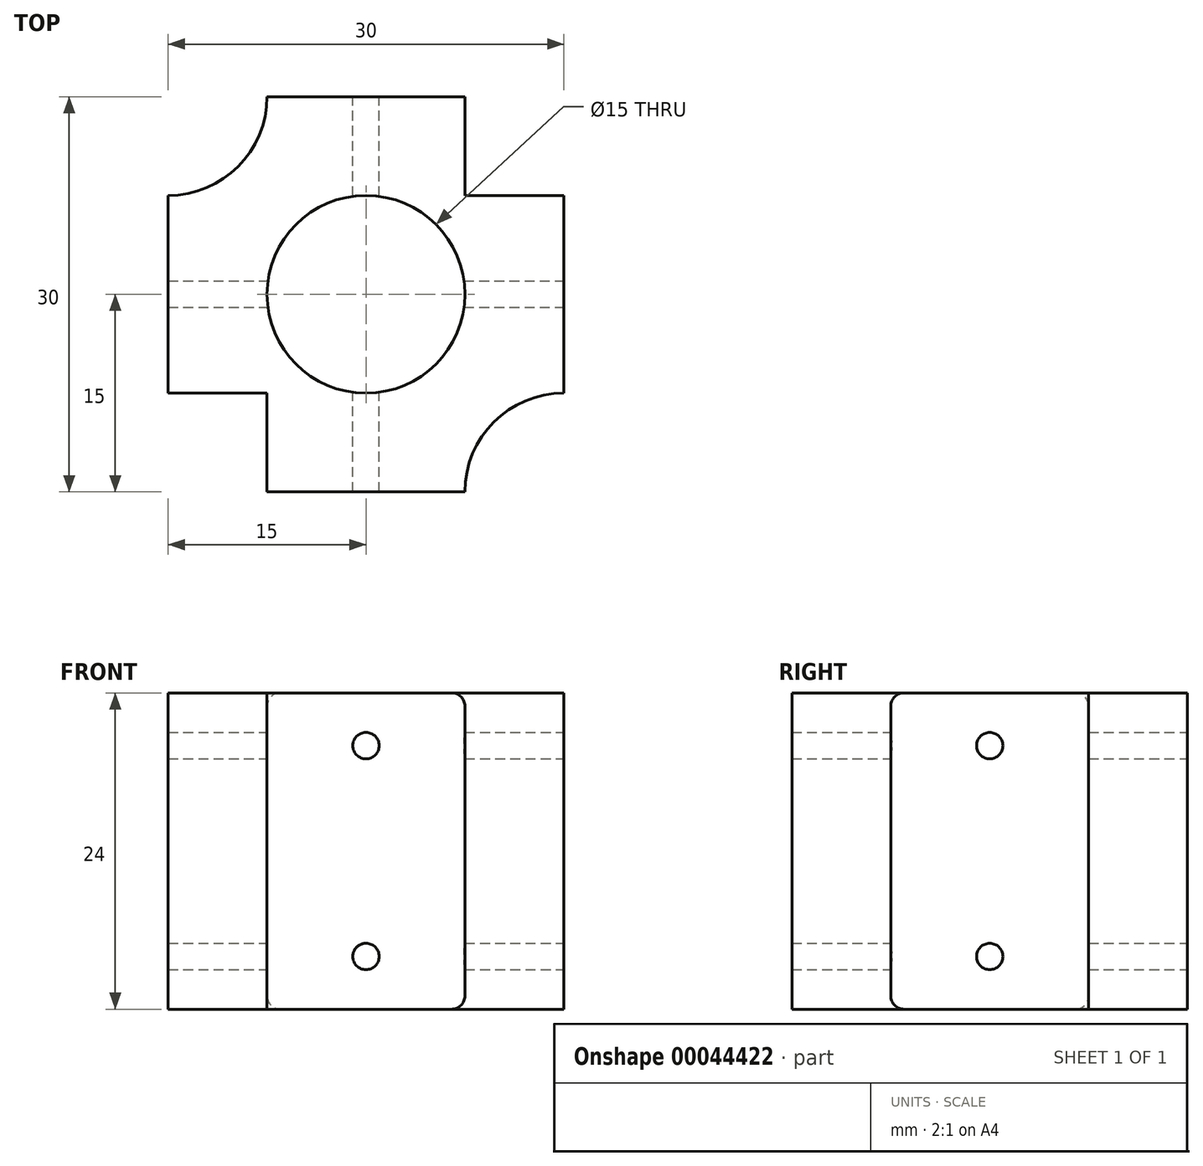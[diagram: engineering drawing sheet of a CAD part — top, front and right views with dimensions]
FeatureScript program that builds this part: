
annotation { "Feature Type Name" : "Feature", "Feature Type Description" : "" }
export const myFeature = defineFeature(function(context is Context, id is Id, definition is map)
    precondition{}
    {
        {
            var Q0;
            Q0=qCreatedBy(makeId("Top.planeOp"),FACE);
            var sketch = newSketch(context, id + "F0", { "sketchPlane" : qUnion([Q0])});
            skLineSegment(sketch, "E0.rect.bottom", {"start": v(15, -7.5) * mm, "end": v(-15, -7.5) * mm});
            skLineSegment(sketch, "E0.rect.top", {"start": v(15, 7.5) * mm, "end": v(-15, 7.5) * mm});
            skLineSegment(sketch, "E0.rect.left", {"start": v(15, -7.5) * mm, "end": v(15, 7.5) * mm});
            skLineSegment(sketch, "E0.rect.right", {"start": v(-15, -7.5) * mm, "end": v(-15, 7.5) * mm});
            skPoint(sketch, "E0.rect.middle", {"position": v(0, 0) * mm});
            skLineSegment(sketch, "E1.rect.bottom", {"start": v(7.5, 15) * mm, "end": v(-7.5, 15) * mm});
            skLineSegment(sketch, "E1.rect.top", {"start": v(7.5, -15) * mm, "end": v(-7.5, -15) * mm});
            skLineSegment(sketch, "E1.rect.left", {"start": v(7.5, 15) * mm, "end": v(7.5, -15) * mm});
            skLineSegment(sketch, "E1.rect.right", {"start": v(-7.5, 15) * mm, "end": v(-7.5, -15) * mm});
            skArc(sketch, "E2", {"start": v(-15, 7.5) * mm, "mid": v(-9.7, 9.7) * mm, "end": v(-7.5, 15) * mm});
            skArc(sketch, "E3.MirrorCS", {"start": v(15, 7.5) * mm, "mid": v(9.7, 9.7) * mm, "end": v(7.5, 15) * mm});
            skArc(sketch, "E4.MirrorCS", {"start": v(-15, -7.5) * mm, "mid": v(-9.7, -9.7) * mm, "end": v(-7.5, -15) * mm});
            skArc(sketch, "E5.MirrorCS", {"start": v(15, -7.5) * mm, "mid": v(9.7, -9.7) * mm, "end": v(7.5, -15) * mm});
            skSolve(sketch);
        }
        {
            var Q0;
            {var subQ0=sQuery(id+"F0.wireOp",EDGE,"E2");Q0=makeQuery(id+"F0.imprint","IMPRINT",FACE,{"disambiguationData":[TD([[makeQuery(id+"F0.imprint","IMPRINT",EDGE,{"derivedFrom":subQ0}),-1.0]])]});}
            var Q1;
            {var subQ3=sQuery(id+"F0.wireOp",EDGE,"E1.rect.bottom");Q1=makeQuery(id+"F0.imprint","IMPRINT",FACE,{"disambiguationData":[TD([[makeQuery(id+"F0.imprint","IMPRINT",EDGE,{"derivedFrom":subQ3}),1.0]])]});}
            var Q2;
            {var subQ3=sQuery(id+"F0.wireOp",EDGE,"E3.MirrorCS");Q2=makeQuery(id+"F0.imprint","IMPRINT",FACE,{"disambiguationData":[TD([[makeQuery(id+"F0.imprint","IMPRINT",EDGE,{"derivedFrom":subQ3}),1.0]])]});}
            var Q3;
            {var subQ5=sQuery(id+"F0.wireOp",EDGE,"E0.rect.left");Q3=makeQuery(id+"F0.imprint","IMPRINT",FACE,{"disambiguationData":[TD([[makeQuery(id+"F0.imprint","IMPRINT",EDGE,{"derivedFrom":subQ5}),1.0]])]});}
            var Q4;
            {var subQ3=sQuery(id+"F0.wireOp",EDGE,"E1.rect.top");Q4=makeQuery(id+"F0.imprint","IMPRINT",FACE,{"disambiguationData":[TD([[makeQuery(id+"F0.imprint","IMPRINT",EDGE,{"derivedFrom":subQ3}),-1.0]])]});}
            var Q5;
            {var subQ0=sQuery(id+"F0.wireOp",EDGE,"E5.MirrorCS");Q5=makeQuery(id+"F0.imprint","IMPRINT",FACE,{"disambiguationData":[TD([[makeQuery(id+"F0.imprint","IMPRINT",EDGE,{"derivedFrom":subQ0}),-1.0]])]});}
            var Q6;
            {var subQ3=sQuery(id+"F0.wireOp",EDGE,"E4.MirrorCS");Q6=makeQuery(id+"F0.imprint","IMPRINT",FACE,{"disambiguationData":[TD([[makeQuery(id+"F0.imprint","IMPRINT",EDGE,{"derivedFrom":subQ3}),1.0]])]});}
            var Q7;
            {var subQ5=sQuery(id+"F0.wireOp",EDGE,"E0.rect.right");Q7=makeQuery(id+"F0.imprint","IMPRINT",FACE,{"disambiguationData":[TD([[makeQuery(id+"F0.imprint","IMPRINT",EDGE,{"derivedFrom":subQ5}),-1.0]])]});}
            var Q8;
            {var subQ3=sQuery(id+"F0.wireOp",EDGE,"E0.rect.bottom");var subQ5=sQuery(id+"F0.wireOp",EDGE,"E1.rect.left");var subQ7=makeQuery(id+"F0.imprint","INTERSECT",VERTEX,{"derivedFrom":[subQ3,subQ5]});Q8=makeQuery(id+"F0.imprint","IMPRINT",FACE,{"disambiguationData":[TD([[makeQuery(id+"F0.imprint","IMPRINT",EDGE,{"disambiguationData":[TD([[subQ7,-1.0]])],"derivedFrom":subQ3}),-1.0]])]});}
            extrude(context, id + "F1", {"entities" : qUnion([Q0, Q1, Q2, Q3, Q4, Q5, Q6, Q7, Q8]), "depth" : 24 * mm, "symmetric" : true});
        }
        {
            var Q0;
            Q0=makeQuery(id+"F1.opExtrude","SWEPT_FACE",FACE,{"disambiguationData":[OSD([sQuery(id+"F0.wireOp",EDGE,"E1.rect.top")])]});
            var sketch = newSketch(context, id + "F2", { "sketchPlane" : qUnion([Q0])});
            skPoint(sketch, "E6", {"position": v(0, 8) * mm});
            skPoint(sketch, "E7.MirrorP", {"position": v(0, -8) * mm});
            skSolve(sketch);
        }
        {
            var Q0;
            Q0=sQuery(id+"F2.wireOp",VERTEX,"E6");
            var Q1;
            Q1=sQuery(id+"F2.wireOp",VERTEX,"E7.MirrorP");
            var Q2;
            Q2=makeQuery(id+"F1.opExtrude","SWEPT_BODY",BODY,{"disambiguationData":[OSD([sQuery(id+"F0.wireOp",EDGE,"E0.rect.left"),sQuery(id+"F0.wireOp",EDGE,"E0.rect.right"),sQuery(id+"F0.wireOp",EDGE,"E1.rect.bottom"),sQuery(id+"F0.wireOp",EDGE,"E1.rect.top"),sQuery(id+"F0.wireOp",EDGE,"E2"),sQuery(id+"F0.wireOp",EDGE,"E3.MirrorCS"),sQuery(id+"F0.wireOp",EDGE,"E4.MirrorCS"),sQuery(id+"F0.wireOp",EDGE,"E5.MirrorCS")])]});
            hole(context, id + "F3", {"style" : HoleStyle.SIMPLE, "holeDiameter" : 2 * mm, "endStyle" : HoleEndStyle.THROUGH, "locations" : qUnion([Q0, Q1]), "scope" : qUnion([Q2])});
        }
        {
            var Q0;
            Q0=makeQuery(id+"F1.opExtrude","CAP_FACE",FACE,{"disambiguationData":[OSD([sQuery(id+"F0.wireOp",EDGE,"E0.rect.left"),sQuery(id+"F0.wireOp",EDGE,"E0.rect.right"),sQuery(id+"F0.wireOp",EDGE,"E1.rect.bottom"),sQuery(id+"F0.wireOp",EDGE,"E1.rect.top"),sQuery(id+"F0.wireOp",EDGE,"E2"),sQuery(id+"F0.wireOp",EDGE,"E3.MirrorCS"),sQuery(id+"F0.wireOp",EDGE,"E4.MirrorCS"),sQuery(id+"F0.wireOp",EDGE,"E5.MirrorCS")])],"isStart":false});
            var sketch = newSketch(context, id + "F4", { "sketchPlane" : qUnion([Q0])});
            skPoint(sketch, "E8.0", {"position": v(0, 0) * mm});
            skSolve(sketch);
        }
        {
            var Q0;
            Q0=sQuery(id+"F4.wireOp",VERTEX,"E8.0");
            var Q1;
            Q1=makeQuery(id+"F1.opExtrude","SWEPT_BODY",BODY,{"disambiguationData":[OSD([sQuery(id+"F0.wireOp",EDGE,"E0.rect.left"),sQuery(id+"F0.wireOp",EDGE,"E0.rect.right"),sQuery(id+"F0.wireOp",EDGE,"E1.rect.bottom"),sQuery(id+"F0.wireOp",EDGE,"E1.rect.top"),sQuery(id+"F0.wireOp",EDGE,"E2"),sQuery(id+"F0.wireOp",EDGE,"E3.MirrorCS"),sQuery(id+"F0.wireOp",EDGE,"E4.MirrorCS"),sQuery(id+"F0.wireOp",EDGE,"E5.MirrorCS")])]});
            hole(context, id + "F5", {"style" : HoleStyle.SIMPLE, "holeDiameter" : 15 * mm, "endStyle" : HoleEndStyle.THROUGH, "locations" : qUnion([Q0]), "scope" : qUnion([Q1])});
        }
        {
            var Q0;
            Q0=makeQuery(id+"F1.opExtrude","SWEPT_FACE",FACE,{"disambiguationData":[OSD([sQuery(id+"F0.wireOp",EDGE,"E0.rect.right")])]});
            var sketch = newSketch(context, id + "F6", { "sketchPlane" : qUnion([Q0])});
            skPoint(sketch, "E9", {"position": v(0, -8) * mm});
            skPoint(sketch, "E10.MirrorP", {"position": v(0, 8) * mm});
            skSolve(sketch);
        }
        {
            var Q0;
            Q0=sQuery(id+"F6.wireOp",VERTEX,"E9");
            var Q1;
            Q1=sQuery(id+"F6.wireOp",VERTEX,"E10.MirrorP");
            var Q2;
            Q2=makeQuery(id+"F1.opExtrude","SWEPT_BODY",BODY,{"disambiguationData":[OSD([sQuery(id+"F0.wireOp",EDGE,"E0.rect.left"),sQuery(id+"F0.wireOp",EDGE,"E0.rect.right"),sQuery(id+"F0.wireOp",EDGE,"E1.rect.bottom"),sQuery(id+"F0.wireOp",EDGE,"E1.rect.top"),sQuery(id+"F0.wireOp",EDGE,"E2"),sQuery(id+"F0.wireOp",EDGE,"E3.MirrorCS"),sQuery(id+"F0.wireOp",EDGE,"E4.MirrorCS"),sQuery(id+"F0.wireOp",EDGE,"E5.MirrorCS")])]});
            hole(context, id + "F7", {"style" : HoleStyle.SIMPLE, "holeDiameter" : 2 * mm, "endStyle" : HoleEndStyle.THROUGH, "locations" : qUnion([Q0, Q1]), "scope" : qUnion([Q2])});
        }
        {
            var Q0;
            Q0=makeQuery(id+"F1.opExtrude","CAP_EDGE",EDGE,{"disambiguationData":[OSD([sQuery(id+"F0.wireOp",EDGE,"E2")])],"isStart":false});
            var Q1;
            Q1=makeQuery(id+"F1.opExtrude","CAP_EDGE",EDGE,{"disambiguationData":[OSD([sQuery(id+"F0.wireOp",EDGE,"E4.MirrorCS")])],"isStart":false});
            var Q2;
            Q2=makeQuery(id+"F1.opExtrude","CAP_EDGE",EDGE,{"disambiguationData":[OSD([sQuery(id+"F0.wireOp",EDGE,"E5.MirrorCS")])],"isStart":false});
            var Q3;
            Q3=makeQuery(id+"F1.opExtrude","CAP_EDGE",EDGE,{"disambiguationData":[OSD([sQuery(id+"F0.wireOp",EDGE,"E3.MirrorCS")])],"isStart":false});
            var Q4;
            Q4=makeQuery(id+"F1.opExtrude","CAP_EDGE",EDGE,{"disambiguationData":[OSD([sQuery(id+"F0.wireOp",EDGE,"E4.MirrorCS")])],"isStart":true});
            var Q5;
            Q5=makeQuery(id+"F1.opExtrude","CAP_EDGE",EDGE,{"disambiguationData":[OSD([sQuery(id+"F0.wireOp",EDGE,"E5.MirrorCS")])],"isStart":true});
            var Q6;
            Q6=makeQuery(id+"F1.opExtrude","CAP_EDGE",EDGE,{"disambiguationData":[OSD([sQuery(id+"F0.wireOp",EDGE,"E3.MirrorCS")])],"isStart":true});
            var Q7;
            Q7=makeQuery(id+"F1.opExtrude","CAP_EDGE",EDGE,{"disambiguationData":[OSD([sQuery(id+"F0.wireOp",EDGE,"E2")])],"isStart":true});
            var Q8;
            Q8=makeQuery(id+"F5.hole-0.boolean.opBoolean","COPY",EDGE,{"derivedFrom":makeQuery(id+"F5.hole-0.opRevolve","SWEPT_EDGE",EDGE,{"disambiguationData":[OSD([sQuery(id+"F5.hole-0.sketch.wireOp",EDGE,"core_line_2"),sQuery(id+"F5.hole-0.sketch.wireOp",EDGE,"core_line_3")])]})});
            var Q9;
            Q9=makeQuery(id+"F5.hole-0.boolean.opBoolean","INTERSECT",EDGE,{"derivedFrom":[makeQuery(id+"F1.opExtrude","CAP_FACE",FACE,{"disambiguationData":[OSD([sQuery(id+"F0.wireOp",EDGE,"E0.rect.left"),sQuery(id+"F0.wireOp",EDGE,"E0.rect.right"),sQuery(id+"F0.wireOp",EDGE,"E1.rect.bottom"),sQuery(id+"F0.wireOp",EDGE,"E1.rect.top"),sQuery(id+"F0.wireOp",EDGE,"E2"),sQuery(id+"F0.wireOp",EDGE,"E3.MirrorCS"),sQuery(id+"F0.wireOp",EDGE,"E4.MirrorCS"),sQuery(id+"F0.wireOp",EDGE,"E5.MirrorCS")])],"isStart":true}),makeQuery(id+"F5.hole-0.opRevolve","SWEPT_FACE",FACE,{"disambiguationData":[OSD([sQuery(id+"F5.hole-0.sketch.wireOp",EDGE,"core_line_2")])]})]});
            fillet(context, id + "F8", {"entities" : qUnion([Q0, Q1, Q2, Q3, Q4, Q5, Q6, Q7, Q8, Q9]), "radius" : 1 * mm, "tangentPropagation" : true, "allowEdgeOverflow" : false});
        }
    });
